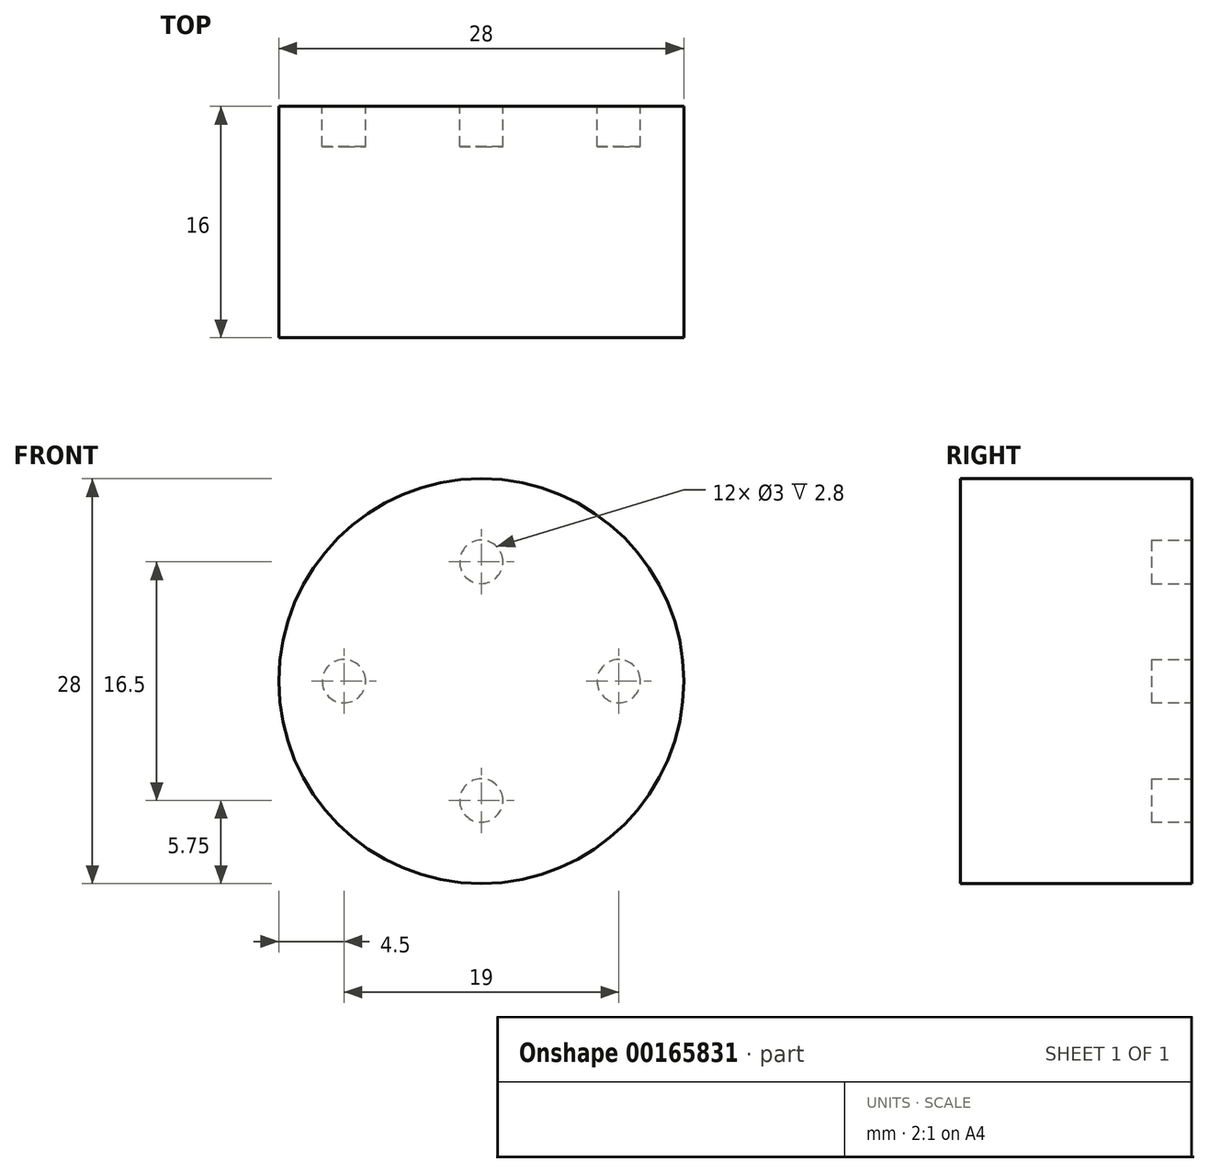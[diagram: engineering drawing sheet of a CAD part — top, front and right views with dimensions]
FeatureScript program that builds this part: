
annotation { "Feature Type Name" : "Feature", "Feature Type Description" : "" }
export const myFeature = defineFeature(function(context is Context, id is Id, definition is map)
    precondition{}
    {
        {
            var Q0;
            Q0=qCreatedBy(makeId("Front.planeOp"),FACE);
            var sketch = newSketch(context, id + "F0", { "sketchPlane" : qUnion([Q0])});
            skCircle(sketch, "E0", {"center": v(0, 0) * mm, "radius": 14 * mm});
            skSolve(sketch);
        }
        {
            var Q0;
            Q0=makeQuery(id+"F0.imprint","IMPRINT",FACE,{"disambiguationData":[TD([[makeQuery(id+"F0.imprint","IMPRINT",EDGE,{"derivedFrom":sQuery(id+"F0.wireOp",EDGE,"E0")}),1.0]])]});
            extrude(context, id + "F1", {"entities" : qUnion([Q0]), "endBound" : BoundingType.SYMMETRIC, "depth" : 16 * mm});
        }
        {
            var Q0;
            Q0=makeQuery(id+"F1.opExtrude","CAP_FACE",FACE,{"disambiguationData":[OSD([sQuery(id+"F0.wireOp",EDGE,"E0")])],"isStart":true});
            var sketch = newSketch(context, id + "F2", { "sketchPlane" : qUnion([Q0])});
            skCircle(sketch, "E1", {"center": v(0, 8.25) * mm, "radius": 1.5 * mm});
            skCircle(sketch, "E2", {"center": v(0, -8.25) * mm, "radius": 1.5 * mm});
            skCircle(sketch, "E3", {"center": v(9.5, 0) * mm, "radius": 1.5 * mm});
            skCircle(sketch, "E4", {"center": v(-9.5, 0) * mm, "radius": 1.5 * mm});
            skSolve(sketch);
        }
        {
            var Q0;
            Q0 = qSketchRegion(id + "F2", true);
            extrude(context, id + "F3", {"entities" : qUnion([Q0]), "operationType" : NewBodyOperationType.REMOVE, "oppositeDirection" : true, "depth" : 2.8 * mm});
        }
    });
